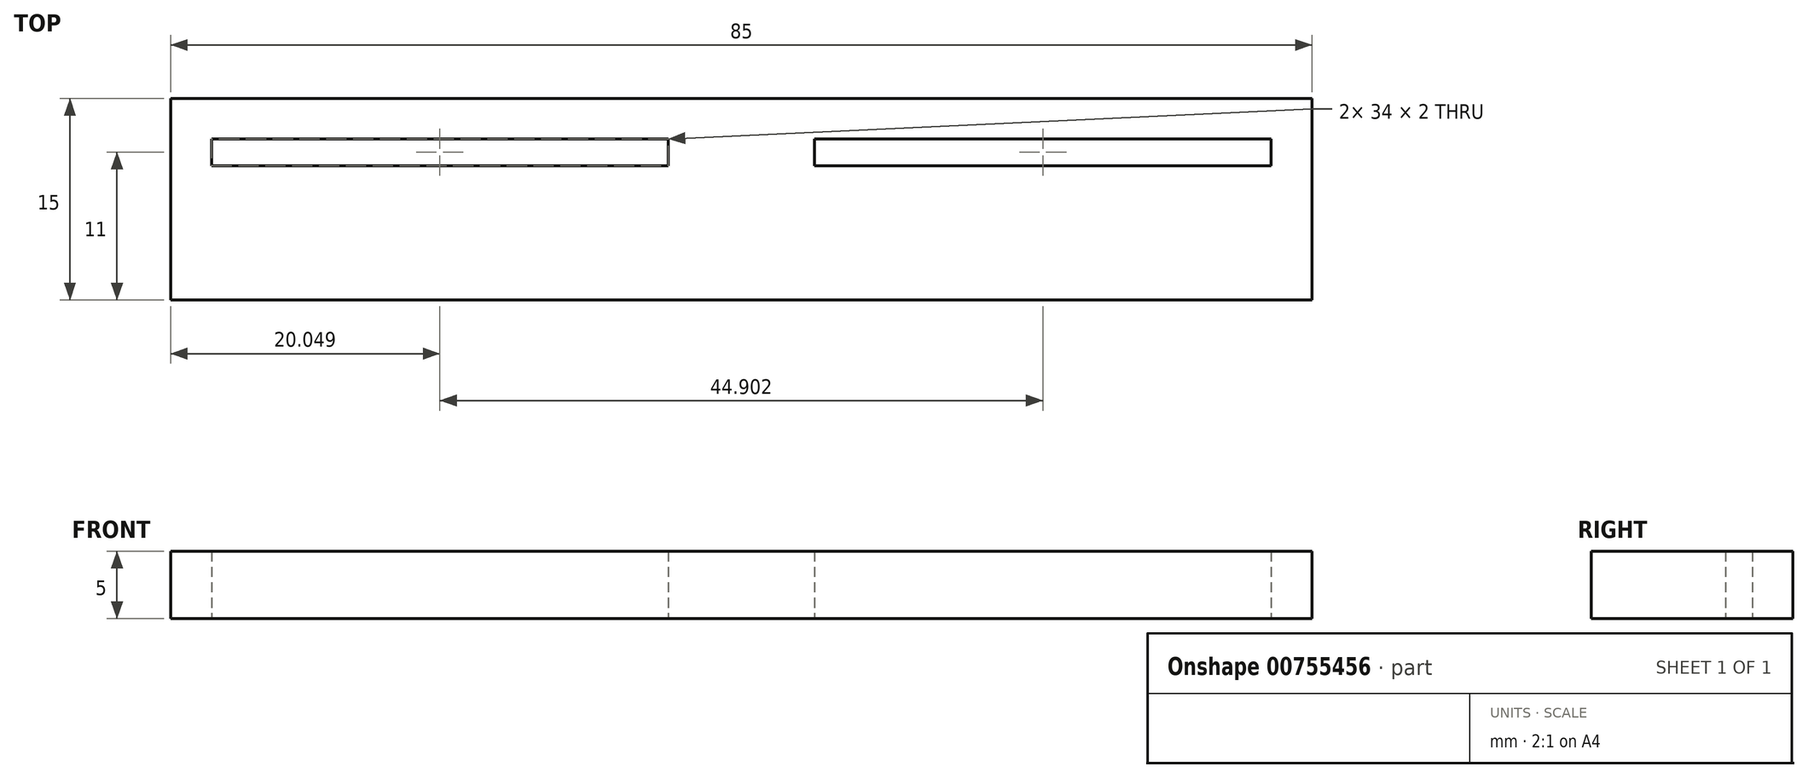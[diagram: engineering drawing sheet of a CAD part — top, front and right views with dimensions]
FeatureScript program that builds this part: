
annotation { "Feature Type Name" : "Feature", "Feature Type Description" : "" }
export const myFeature = defineFeature(function(context is Context, id is Id, definition is map)
    precondition{}
    {
        {
            var Q0;
            Q0=qCreatedBy(makeId("Top.planeOp"),FACE);
            var sketch = newSketch(context, id + "F0", { "sketchPlane" : qUnion([Q0])});
            skLineSegment(sketch, "E0.bottom", {"start": v(42.5, -7.5) * mm, "end": v(-42.5, -7.5) * mm});
            skLineSegment(sketch, "E0.top", {"start": v(42.5, 7.5) * mm, "end": v(-42.5, 7.5) * mm});
            skLineSegment(sketch, "E0.left", {"start": v(42.5, -7.5) * mm, "end": v(42.5, 7.5) * mm});
            skLineSegment(sketch, "E0.right", {"start": v(-42.5, -7.5) * mm, "end": v(-42.5, 7.5) * mm});
            skPoint(sketch, "E0.middle", {"position": v(0, 0) * mm});
            skSolve(sketch);
        }
        {
            var Q0;
            Q0 = qSketchRegion(id + "F0", true);
            extrude(context, id + "F1", {"entities" : qUnion([Q0]), "depth" : 5 * mm, "offsetDistance" : 25 * mm});
        }
        {
            var Q0;
            Q0=qCreatedBy(makeId("Top.planeOp"),FACE);
            var sketch = newSketch(context, id + "F2", { "sketchPlane" : qUnion([Q0])});
            skLineSegment(sketch, "E1.bottom", {"start": v(-39.45, 4.5) * mm, "end": v(-5.45, 4.5) * mm});
            skLineSegment(sketch, "E1.top", {"start": v(-39.45, 2.5) * mm, "end": v(-5.45, 2.5) * mm});
            skLineSegment(sketch, "E1.left", {"start": v(-39.45, 4.5) * mm, "end": v(-39.45, 2.5) * mm});
            skLineSegment(sketch, "E1.right", {"start": v(-5.45, 4.5) * mm, "end": v(-5.45, 2.5) * mm});
            skLineSegment(sketch, "E2", {"start": v(0, 24.53) * mm, "end": v(0, -18.35) * mm, "construction": true});
            skLineSegment(sketch, "E3.MirrorCS", {"start": v(39.45, 4.5) * mm, "end": v(5.45, 4.5) * mm});
            skLineSegment(sketch, "E4.MirrorCS", {"start": v(39.45, 2.5) * mm, "end": v(5.45, 2.5) * mm});
            skLineSegment(sketch, "E5.MirrorCS", {"start": v(5.45, 4.5) * mm, "end": v(5.45, 2.5) * mm});
            skLineSegment(sketch, "E6.MirrorCS", {"start": v(39.45, 4.5) * mm, "end": v(39.45, 2.5) * mm});
            skSolve(sketch);
        }
        {
            var Q0;
            Q0 = qSketchRegion(id + "F2", true);
            extrude(context, id + "F3", {"entities" : qUnion([Q0]), "operationType" : NewBodyOperationType.REMOVE, "endBound" : BoundingType.THROUGH_ALL, "depth" : 25 * mm, "offsetDistance" : 25 * mm});
        }
    });
